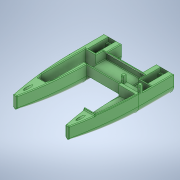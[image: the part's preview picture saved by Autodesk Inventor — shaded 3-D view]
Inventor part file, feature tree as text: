
AUTODESK INVENTOR PART (.ipt)
format: ipt  version: 2020.3 (Build 243373000, 373)  size: 1,118,720 bytes
history: native  units: mm
features: sketch x22, extrude x20, other x15, reference x13, chamfer x11, projected_geometry x11, plane x9, mirror x4, fillet x4, loft x1, direct_edit x1
ambient origin geometry x8: Origin, YZ Plane, XZ Plane, XY Plane, X Axis, Y Axis, Z Axis, Center Point
bodies: Solid1 (feature_tree)
feature tree (111):
  other  "Blocks"
  sketch  "Sketch1"  dims[d0=100.0mm d1=240.0mm]
  plane  "Work Plane1"
  plane  "Work Plane2"
  plane  "Work Plane3"
  plane  "Work Plane4"
  extrude  "Extrusion1"  Depth=240.0mm
  loft  "Loft3"
  chamfer  "Chamfer1"  Distance=10.0mm
  plane  "Work Plane7"
  mirror  "Mirror1"
  extrude  "Extrusion2"  Depth=13.217565mm
  extrude  "Extrusion3"  Depth=12.5mm
  extrude  "Extrusion4"  Depth=7.930539mm
  extrude  "Extrusion5"  Depth=10.0mm
  extrude  "Extrusion6"  Depth=3.0mm
  mirror  "Mirror2"
  plane  "Work Plane9"
  extrude  "Extrusion7"  Depth=5.0mm
  mirror  "Mirror3"
  extrude  "Extrusion8"  TaperAngle=0.0deg  [1 undecoded]
  extrude  "Extrusion9"  Depth=2.0mm TaperAngle=45.0deg
  chamfer  "Chamfer2"  Distance=10.0mm
  direct_edit  "Direct Edit1"
  extrude  "Extrusion10"  Depth=42.0mm
  extrude  "Extrusion11"  Depth=10.0mm TaperAngle=0.0deg
  extrude  "Extrusion12"  Depth=8.0mm
  extrude  "Extrusion13"  Depth=10.0mm TaperAngle=0.0deg
  extrude  "Extrusion14"  Depth=10.0mm
  plane  "Work Plane12"
  extrude  "Extrusion15"  Depth=10.0mm
  extrude  "Extrusion16"  Depth=10.0mm TaperAngle=0.0deg
  extrude  "Extrusion17"  TaperAngle=75.0deg  [1 undecoded]
  extrude  "Extrusion18"  Depth=10.0mm
  mirror  "Mirror5"
  fillet  "Fillet2"  Radius=10.0mm
  chamfer  "Chamfer3"  Distance=254.929mm
  fillet  "Fillet3"  Radius=10.0mm
  fillet  "Fillet4"  Radius=13.0mm
  chamfer  "Chamfer4"  Distance=140.0mm
  chamfer  "Chamfer5"  Distance=30.0mm
  chamfer  "Chamfer6"  Distance=3.0mm
  extrude  "Extrusion19"  Depth=10.0mm
  chamfer  "Chamfer7"  Distance=5.0mm
  chamfer  "Chamfer8"  Distance=15.0mm
  chamfer  "Chamfer9"  Distance=35.0mm
  fillet  "Fillet5"  Radius=2.5mm
  chamfer  "Chamfer10"  Distance=28.0mm
  chamfer  "Chamfer11"  Distance=8.0mm
  plane  "Work Plane14"
  extrude  "Extrusion20"  Depth=10.0mm TaperAngle=0.0deg
  sketch  "Sketch3"  dims[d2=280.0mm d3=30.0mm]
  sketch  "Sketch4"  dims[d4=50.0mm]
  other  "Edges3"
  plane  "Work Plane5"
  sketch  "Sketch5"  dims[d5=30.0mm]
  projected_geometry  "Projected Loop2"
  sketch  "Sketch6"  dims[d7=18.0mm]
  other  "Prindere servo"
  sketch  "Sketch7"  dims[d8=25.0mm]
  projected_geometry  "Projected Loop3"
  sketch  "Sketch8"  dims[d9=18.0mm]
  sketch  "Sketch9"  dims[d10=25.0mm d11=10.0mm d12=0.0mm]
  projected_geometry  "Projected Loop4"
  sketch  "Sketch12"  dims[d13=25.0mm d14=13.217565mm]
  sketch  "Sketch13"  dims[d16=7.930539mm d17=12.5mm]
  sketch  "Sketch14"  dims[d18=12.5mm d19=7.930539mm]
  sketch  "Sketch15"  dims[d24=10.0mm d25=5.0mm]
  sketch  "Sketch17"  dims[d26=3.0mm d27=3.0mm]
  reference  "Reference1"
  reference  "Reference2"
  reference  "Reference3"
  reference  "Reference4"
  reference  "Reference5"
  sketch  "Sketch18"  dims[d28=5.0mm d29=5.0mm]
  reference  "Reference6"
  reference  "Reference7"
  reference  "Reference8"
  reference  "Reference9"
  sketch  "Sketch19"  dims[d35=0.0mm d36=90.0deg d37=0.0mm d38=90.0deg]
  projected_geometry  "Projected Loop5"
  projected_geometry  "Projected Loop6"
  sketch  "Sketch20"  dims[d39=0.0mm d40=90.0deg d42=2.0mm d43=2.0mm d44=45.0deg]
  sketch  "Sketch22"  dims[d46=-100.0mm]
  projected_geometry  "Projected Loop7"
  projected_geometry  "Projected Loop8"
  projected_geometry  "Projected Loop9"
  projected_geometry  "Projected Loop10"
  projected_geometry  "Projected Loop11"
  sketch  "Sketch23"  dims[d47=30.0mm d48=10.0mm d49=0.0mm]
  reference  "Reference10"
  reference  "Reference11"
  sketch  "Sketch24"  dims[d97=22.0mm d98=42.0mm]
  sketch  "Sketch25"  dims[d99=10.0mm d100=45.0mm d101=0.0mm]
  projected_geometry  "Projected Loop12"
  sketch  "Sketch26"  dims[d102=8.0mm d103=8.0mm]
  other  "Work Axis2"
  sketch  "Sketch28"  dims[d104=12.0mm d105=0.0mm d106=40.0mm d107=0.0mm d108=7.0mm d109=20.0mm d110=5.0mm d111=0.0mm d118=75.0deg d119=6.5mm d120=10.0mm d121=254.929mm d122=0.0mm d124=10.0mm d125=13.0mm d126=140.0mm d127=30.0mm d128=3.0mm d129=5.0mm d130=5.0mm d131=15.0mm d132=35.0mm d133=0.0mm d136=2.5mm d137=28.0mm d138=8.0mm d139=25.0mm d140=0.0mm d141=44.0mm d142=2.0mm d143=1.396263mm d145=2.5mm d146=3.0mm d147=0.0mm d148=20.0mm d149=0.0mm d150=10.0mm d151=0.0mm d154=8.5mm d155=8.5mm d156=8.0mm d157=8.0mm d158=100.0mm d159=0.0mm d160=2.5mm d161=2.5mm d162=2.5mm d163=2.5mm d164=27.5mm d165=0.0mm d166=2.5mm d167=2.5mm d168=120.0mm d169=0.0mm d170=5.0mm d171=0.0mm d173=12.0mm d174=5.0mm d175=18.0mm d176=0.0mm d177=10.0mm d178=0.0mm d179=2.0mm d180=2.0mm d181=2.0mm d182=45.0deg d183=0.2mm d184=0.2mm d185=2.0mm d186=2.0mm d187=45.0deg d188=2.0mm d189=2.0mm d190=45.0deg d191=2.0mm d192=2.0mm d193=45.0deg d194=2.5mm d195=0.0mm d196=2.0mm d197=2.0mm d198=45.0deg d199=2.5mm d200=2.0mm d201=45.0deg d202=2.5mm d203=2.0mm d204=45.0deg d205=0.5mm d206=2.5mm d207=2.0mm d208=45.0deg d209=2.5mm d210=2.0mm d211=45.0deg d212=3.0mm d213=3.0mm d214=5.0mm d215=0.0mm]
  reference  "Reference12"
  reference  "Reference13"
  other  "Prindere servo:1"
  other  "Prindere servo:2"
  other  "Prindere servo:3"
  other  "Delete1"
  other  "<userpath>\Documents\Inventor\TheArch\R&D\Beta0\Structura\Prototip\Prototip1.iam"
  other  "Prototip1.iam"
  other  "MG996:3"
  other  "AnsambluMotor:1"
  other  "Prindere:1"
  other  "carma_v0:1"
  other  "carma_v0:2"
note: 2 required parameter values undecoded (feature->parameter linkage not recoverable at this tier; creation-order binding heuristic only, values carry confidence <= 0.55)
